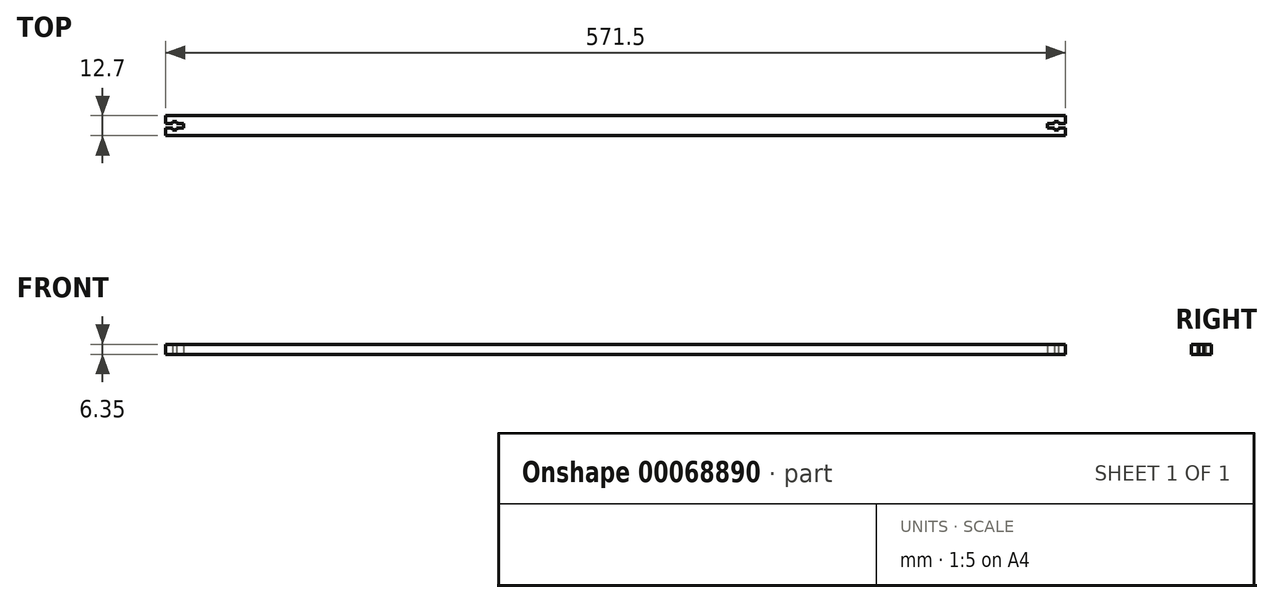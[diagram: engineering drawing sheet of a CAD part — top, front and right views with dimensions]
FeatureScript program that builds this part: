
annotation { "Feature Type Name" : "Feature", "Feature Type Description" : "" }
export const myFeature = defineFeature(function(context is Context, id is Id, definition is map)
    precondition{}
    {
        {
            var Q0;
            Q0=qCreatedBy(makeId("Top.planeOp"),FACE);
            var sketch = newSketch(context, id + "F0", { "sketchPlane" : qUnion([Q0])});
            skLineSegment(sketch, "E0.rect.left", {"start": v(285.75, -6.35) * mm, "end": v(285.75, -1.46) * mm});
            skLineSegment(sketch, "E0.rect.right", {"start": v(-285.75, -6.35) * mm, "end": v(-285.75, -1.46) * mm});
            skPoint(sketch, "E0.rect.middle", {"position": v(0, 0) * mm});
            skLineSegment(sketch, "E1", {"start": v(0, 38.1) * mm, "end": v(0, -38.1) * mm, "construction": true});
            skLineSegment(sketch, "E2", {"start": v(-285.75, 0) * mm, "end": v(285.75, 0) * mm, "construction": true});
            skLineSegment(sketch, "E3.0", {"start": v(-1.46, 38.1) * mm, "end": v(-1.46, -38.1) * mm, "construction": true});
            skLineSegment(sketch, "E4", {"start": v(-1.46, -38.1) * mm, "end": v(-1.46, -33.66) * mm});
            skLineSegment(sketch, "E5", {"start": v(-1.46, -33.66) * mm, "end": v(-2.73, -33.66) * mm});
            skLineSegment(sketch, "E6", {"start": v(-2.73, -33.66) * mm, "end": v(-2.73, -31.12) * mm});
            skLineSegment(sketch, "E7", {"start": v(-2.73, -31.12) * mm, "end": v(-1.46, -31.12) * mm});
            skLineSegment(sketch, "E8", {"start": v(-1.46, -31.12) * mm, "end": v(-1.46, -26.67) * mm});
            skLineSegment(sketch, "E9", {"start": v(-1.46, -26.67) * mm, "end": v(0, -26.67) * mm});
            skLineSegment(sketch, "E10.MirrorCS", {"start": v(1.46, -26.67) * mm, "end": v(0, -26.67) * mm});
            skLineSegment(sketch, "E11.MirrorCS", {"start": v(1.46, -31.12) * mm, "end": v(1.46, -26.67) * mm});
            skLineSegment(sketch, "E12.MirrorCS", {"start": v(2.73, -31.12) * mm, "end": v(1.46, -31.12) * mm});
            skLineSegment(sketch, "E13.MirrorCS", {"start": v(2.73, -33.66) * mm, "end": v(2.73, -31.12) * mm});
            skLineSegment(sketch, "E14.MirrorCS", {"start": v(1.46, -33.66) * mm, "end": v(2.73, -33.66) * mm});
            skLineSegment(sketch, "E15.MirrorCS", {"start": v(1.46, -38.1) * mm, "end": v(1.46, -33.66) * mm});
            skLineSegment(sketch, "E16.0", {"start": v(-285.75, -1.46) * mm, "end": v(298.45, -1.46) * mm, "construction": true});
            skLineSegment(sketch, "E17", {"start": v(-285.75, -1.46) * mm, "end": v(-281.3, -1.46) * mm});
            skLineSegment(sketch, "E18", {"start": v(-281.3, -1.46) * mm, "end": v(-281.3, -2.73) * mm});
            skLineSegment(sketch, "E19", {"start": v(-281.3, -2.73) * mm, "end": v(-278.77, -2.73) * mm});
            skLineSegment(sketch, "E20", {"start": v(-278.77, -2.73) * mm, "end": v(-278.77, -1.46) * mm});
            skLineSegment(sketch, "E21", {"start": v(-278.77, -1.46) * mm, "end": v(-274.32, -1.46) * mm});
            skLineSegment(sketch, "E22", {"start": v(-274.32, -1.46) * mm, "end": v(-274.32, 0) * mm});
            skLineSegment(sketch, "E23.MirrorCS", {"start": v(-274.32, 1.46) * mm, "end": v(-274.32, 0) * mm});
            skLineSegment(sketch, "E24.MirrorCS", {"start": v(-278.77, 1.46) * mm, "end": v(-274.32, 1.46) * mm});
            skLineSegment(sketch, "E25.MirrorCS", {"start": v(-278.77, 2.73) * mm, "end": v(-278.77, 1.46) * mm});
            skLineSegment(sketch, "E26.MirrorCS", {"start": v(-281.3, 2.73) * mm, "end": v(-278.77, 2.73) * mm});
            skLineSegment(sketch, "E27.MirrorCS", {"start": v(-281.3, 1.46) * mm, "end": v(-281.3, 2.73) * mm});
            skLineSegment(sketch, "E28.MirrorCS", {"start": v(-285.75, 1.46) * mm, "end": v(-281.3, 1.46) * mm});
            skLineSegment(sketch, "E29.MirrorCS", {"start": v(285.75, -1.46) * mm, "end": v(281.3, -1.46) * mm});
            skLineSegment(sketch, "E30.MirrorCS", {"start": v(281.3, -1.46) * mm, "end": v(281.3, -2.73) * mm});
            skLineSegment(sketch, "E31.MirrorCS", {"start": v(281.3, -2.73) * mm, "end": v(278.77, -2.73) * mm});
            skLineSegment(sketch, "E32.MirrorCS", {"start": v(278.77, -2.73) * mm, "end": v(278.77, -1.46) * mm});
            skLineSegment(sketch, "E33.MirrorCS", {"start": v(278.77, -1.46) * mm, "end": v(274.32, -1.46) * mm});
            skLineSegment(sketch, "E34.MirrorCS", {"start": v(274.32, -1.46) * mm, "end": v(274.32, 0) * mm});
            skLineSegment(sketch, "E35.MirrorCS", {"start": v(274.32, 1.46) * mm, "end": v(274.32, 0) * mm});
            skLineSegment(sketch, "E36.MirrorCS", {"start": v(278.77, 1.46) * mm, "end": v(274.32, 1.46) * mm});
            skLineSegment(sketch, "E37.MirrorCS", {"start": v(278.77, 2.73) * mm, "end": v(278.77, 1.46) * mm});
            skLineSegment(sketch, "E38.MirrorCS", {"start": v(281.3, 2.73) * mm, "end": v(278.77, 2.73) * mm});
            skLineSegment(sketch, "E39.MirrorCS", {"start": v(281.3, 1.46) * mm, "end": v(281.3, 2.73) * mm});
            skLineSegment(sketch, "E40.MirrorCS", {"start": v(285.75, 1.46) * mm, "end": v(281.3, 1.46) * mm});
            skLineSegment(sketch, "E41.trimOffspring", {"start": v(285.75, 1.46) * mm, "end": v(285.75, 6.35) * mm});
            skLineSegment(sketch, "E42.trimOffspring", {"start": v(-285.75, 1.46) * mm, "end": v(-285.75, 6.35) * mm});
            skCircle(sketch, "E43", {"center": v(0, 34.92) * mm, "radius": 1.46 * mm});
            skLineSegment(sketch, "E44.0", {"start": v(-285.75, -6.35) * mm, "end": v(285.75, -6.35) * mm});
            skLineSegment(sketch, "E45.0", {"start": v(-285.75, 6.35) * mm, "end": v(285.75, 6.35) * mm});
            skPoint(sketch, "E0.rect.bottom.start.orphan", {"position": v(285.75, -38.1) * mm});
            skPoint(sketch, "E46.orphan", {"position": v(-285.75, -38.1) * mm});
            skLineSegment(sketch, "E47.trimOffspring", {"start": v(-285.75, 34.92) * mm, "end": v(-285.75, 38.1) * mm});
            skLineSegment(sketch, "E48.trimOffspring", {"start": v(285.75, 34.93) * mm, "end": v(285.75, 38.1) * mm});
            skSolve(sketch);
        }
        {
            var Q0;
            Q0=makeQuery(id+"F0.imprint","IMPRINT",FACE,{"disambiguationData":[TD([[makeQuery(id+"F0.imprint","IMPRINT",EDGE,{"derivedFrom":sQuery(id+"F0.wireOp",EDGE,"E0.rect.left")}),1.0]])]});
            extrude(context, id + "F1", {"entities" : qUnion([Q0]), "depth" : 6.35 * mm});
        }
    });
